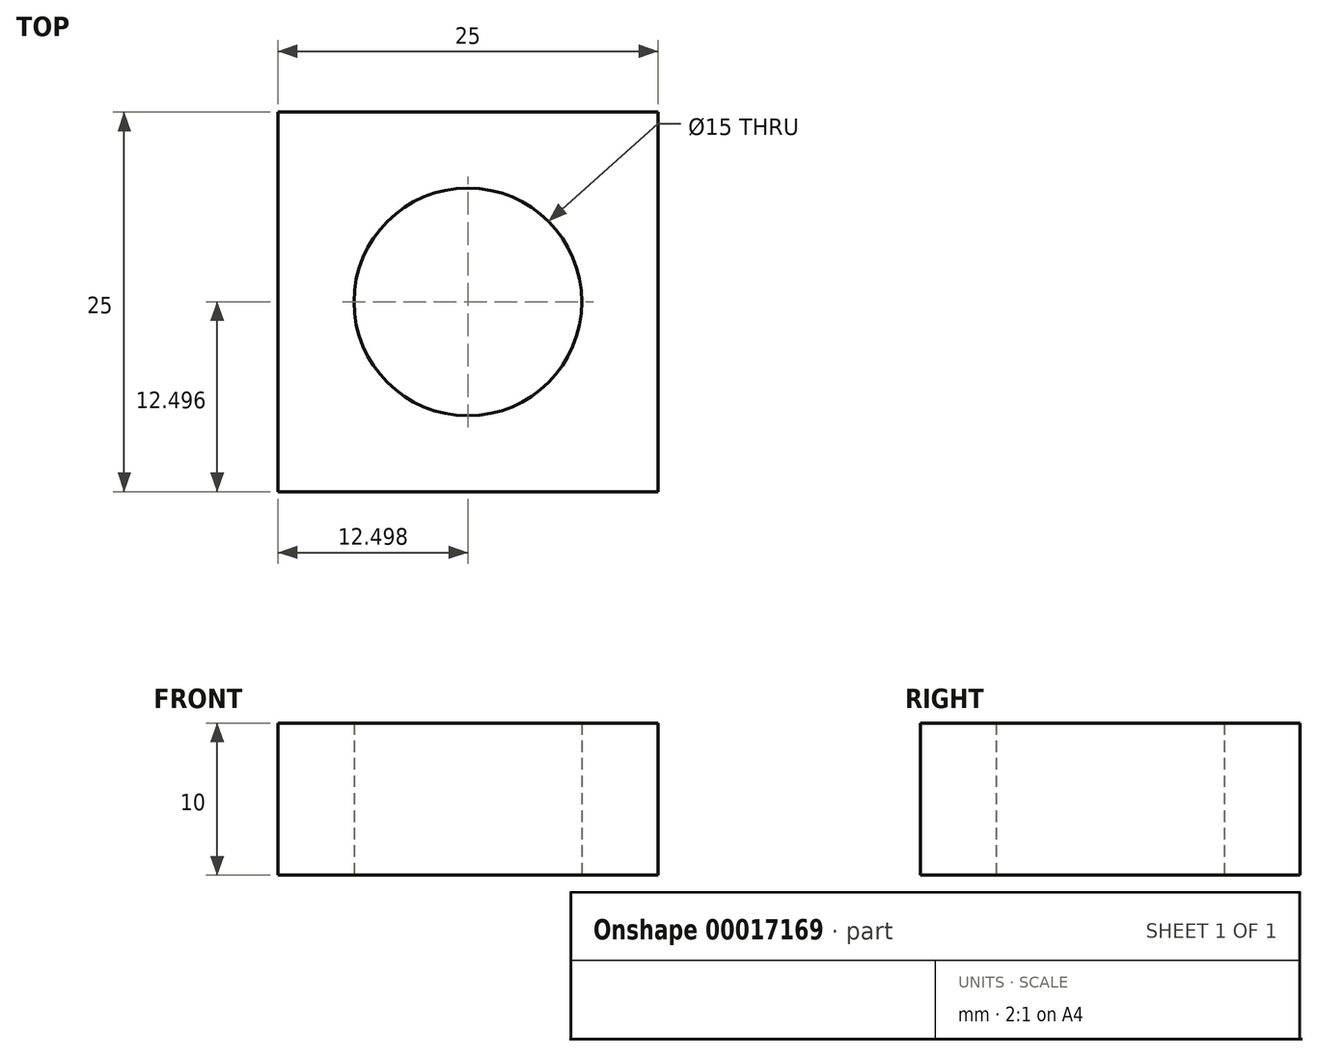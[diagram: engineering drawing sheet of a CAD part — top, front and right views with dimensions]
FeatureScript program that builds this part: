
annotation { "Feature Type Name" : "Feature", "Feature Type Description" : "" }
export const myFeature = defineFeature(function(context is Context, id is Id, definition is map)
    precondition{}
    {
        {
            var Q0;
            Q0=qCreatedBy(makeId("Top.planeOp"),FACE);
            var sketch = newSketch(context, id + "F0", { "sketchPlane" : qUnion([Q0])});
            skLineSegment(sketch, "E0.bottom", {"start": v(-14.11, -10.51) * mm, "end": v(10.89, -10.51) * mm});
            skLineSegment(sketch, "E0.top", {"start": v(-14.11, 14.49) * mm, "end": v(10.89, 14.49) * mm});
            skLineSegment(sketch, "E0.left", {"start": v(-14.11, -10.51) * mm, "end": v(-14.11, 14.49) * mm});
            skLineSegment(sketch, "E0.right", {"start": v(10.89, -10.51) * mm, "end": v(10.89, 14.49) * mm});
            skCircle(sketch, "E1", {"center": v(-1.61, 1.99) * mm, "radius": 7.5 * mm});
            skPoint(sketch, "E2.orphan", {"position": v(10.89, 1.99) * mm});
            skPoint(sketch, "E3.start.orphan", {"position": v(-14.11, 1.99) * mm});
            skSolve(sketch);
        }
        {
            var Q0;
            Q0 = qSketchRegion(id + "F0", true);
            extrude(context, id + "F1", {"entities" : qUnion([Q0]), "depth" : 10 * mm});
        }
        {
            var Q0;
            Q0 = qSketchRegion(id + "F0", true);
            extrude(context, id + "F2", {"entities" : qUnion([Q0]), "operationType" : NewBodyOperationType.ADD, "depth" : 10 * mm});
        }
    });
